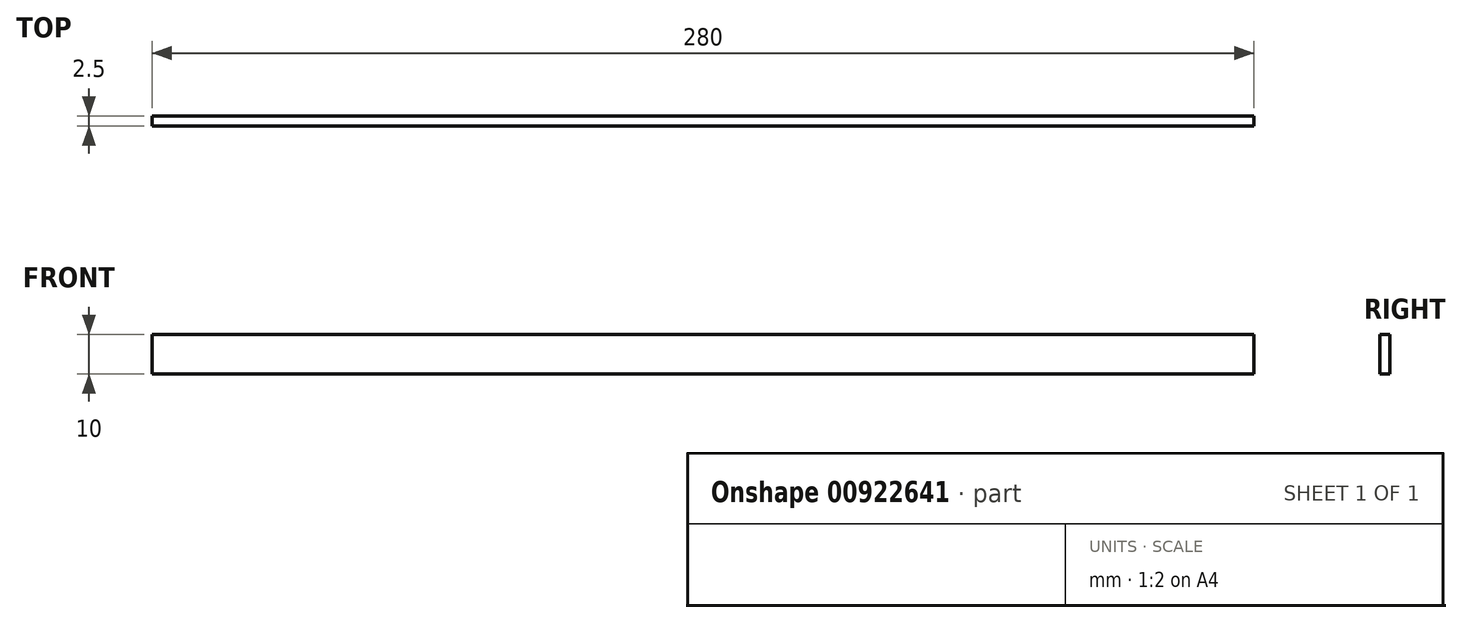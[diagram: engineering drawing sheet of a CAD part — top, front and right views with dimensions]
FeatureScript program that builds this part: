
annotation { "Feature Type Name" : "Feature", "Feature Type Description" : "" }
export const myFeature = defineFeature(function(context is Context, id is Id, definition is map)
    precondition{}
    {
        {
            var Q0;
            Q0=qCreatedBy(makeId("Front.planeOp"),FACE);
            var sketch = newSketch(context, id + "F0", { "sketchPlane" : qUnion([Q0])});
            skLineSegment(sketch, "E0.bottom", {"start": v(139.75, -1.79) * mm, "end": v(-140.25, -1.79) * mm});
            skLineSegment(sketch, "E0.top", {"start": v(139.75, -11.79) * mm, "end": v(-140.25, -11.79) * mm});
            skLineSegment(sketch, "E0.left", {"start": v(139.75, -1.79) * mm, "end": v(139.75, -11.79) * mm});
            skLineSegment(sketch, "E0.right", {"start": v(-140.25, -1.79) * mm, "end": v(-140.25, -11.79) * mm});
            skPoint(sketch, "E0.middle", {"position": v(-0.25, -6.79) * mm});
            skSolve(sketch);
        }
        {
            var Q0;
            Q0 = qSketchRegion(id + "F0", true);
            extrude(context, id + "F1", {"entities" : qUnion([Q0]), "depth" : 2.5 * mm, "offsetDistance" : 25.4 * mm});
        }
    });
